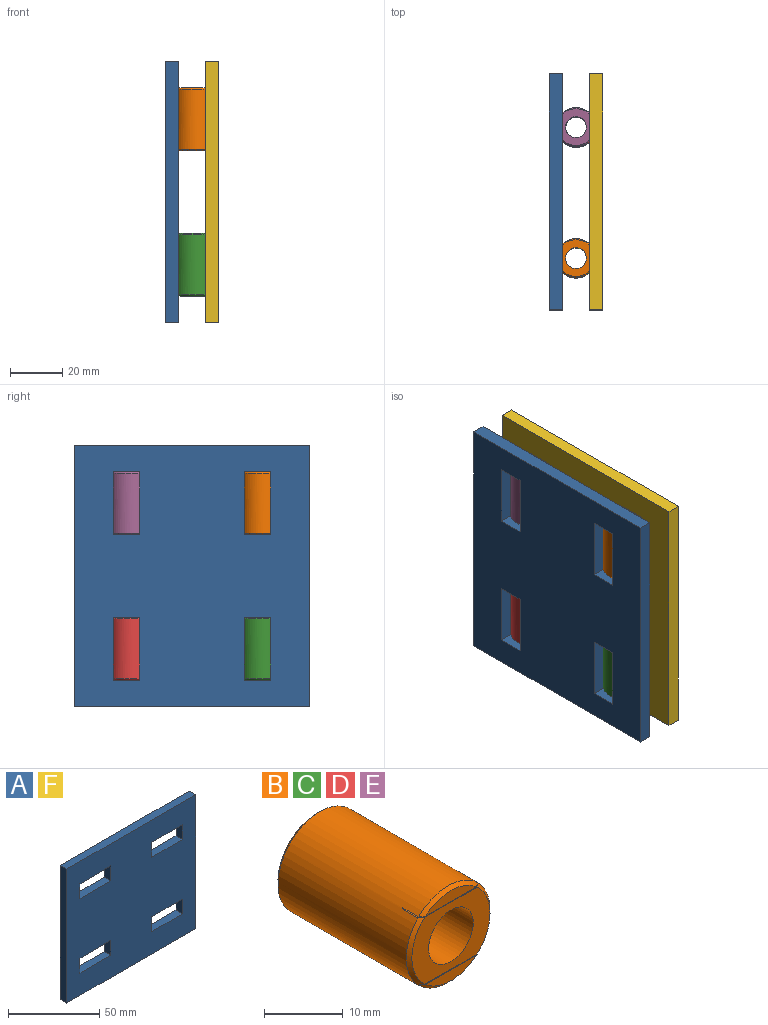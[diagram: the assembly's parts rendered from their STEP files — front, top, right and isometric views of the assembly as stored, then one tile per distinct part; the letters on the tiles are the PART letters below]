
ASSEMBLY  parts=6 mates=7
PART A: 22 faces, bbox 100x5x90 mm
  f0: plane 100x5mm, normal (0,0,1), area 500mm2, adj f1,f19,f20,f21
  f1: plane 90x5mm, normal (-1,0,0), area 450mm2, adj f0,f2,f20,f21
  f2: plane 100x5mm, normal (0,0,-1), area 500mm2, adj f1,f19,f20,f21
  f3: plane 24x5mm, normal (0,0,1), area 120mm2, adj f4,f15,f20,f21
  f4: plane 10x5mm, normal (1,0,0), area 50mm2, adj f3,f5,f20,f21
  f5: plane 24x5mm, normal (0,0,-1), area 120mm2, adj f4,f15,f20,f21
  f6: plane 24x5mm, normal (0,0,1), area 120mm2, adj f7,f16,f20,f21
  f7: plane 10x5mm, normal (1,0,0), area 50mm2, adj f6,f8,f20,f21
  f8: plane 24x5mm, normal (0,0,-1), area 120mm2, adj f7,f16,f20,f21
  f9: plane 24x5mm, normal (0,0,-1), area 120mm2, adj f10,f17,f20,f21
  f10: plane 10x5mm, normal (-1,0,0), area 50mm2, adj f9,f11,f20,f21
  f11: plane 24x5mm, normal (0,0,1), area 120mm2, adj f10,f17,f20,f21
  f12: plane 24x5mm, normal (0,0,1), area 120mm2, adj f13,f18,f20,f21
  f13: plane 10x5mm, normal (1,0,0), area 50mm2, adj f12,f14,f20,f21
  f14: plane 24x5mm, normal (0,0,-1), area 120mm2, adj f13,f18,f20,f21
  f15: plane 10x5mm, normal (-1,0,0), area 50mm2, adj f3,f5,f20,f21
  f16: plane 10x5mm, normal (-1,0,0), area 50mm2, adj f6,f8,f20,f21
  f17: plane 10x5mm, normal (1,0,0), area 50mm2, adj f9,f11,f20,f21
  f18: plane 10x5mm, normal (-1,0,0), area 50mm2, adj f12,f14,f20,f21
  f19: plane 90x5mm, normal (1,0,0), area 450mm2, adj f0,f2,f20,f21
  f20: plane 100x90mm, normal (0,-1,0), area 8040mm2, adj f0,f1,f2,f3,f4,f5,f6,f7
  f21: plane 100x90mm, normal (0,1,0), area 8040mm2, adj f0,f1,f2,f3,f4,f5,f6,f7
PART B: 17 faces, bbox 15x24x15 mm
  f0: plane 9.15x1.7mm, normal (0,-1,0), area 10.6mm2, adj f1,f16
  f1: cone r=7mm half-angle=45deg, axis (0,1,0), area 7.7mm2, adj f0,f6,f16
  f2: cone r=7mm half-angle=45deg, axis (0,1,0), area 8.2mm2, adj f6,f7,f12,f15
  f3: plane 9.15x1.7mm, normal (0,-1,0), area 10.6mm2, adj f4,f13
  f4: cone r=7mm half-angle=45deg, axis (0,1,0), area 7.7mm2, adj f3,f6,f13
  f5: cylinder r=4mm len=24mm, axis (0,1,0), area 603.2mm2, adj f7,f8
  f6: cylinder r=7.5mm len=23mm, axis (0,1,0), area 1082.3mm2, adj f1,f2,f4,f9,f10,f11,f12,f13
  f7: plane 14x10.4mm, normal (0,-1,0), area 80.5mm2, adj f2,f5,f9,f12,f15
  f8: plane 14x14mm, normal (0,1,0), area 103.7mm2, adj f5,f10
  f9: cone r=7mm half-angle=45deg, axis (0,1,0), area 8.2mm2, adj f6,f7,f12,f15
  f10: cone r=7.5mm half-angle=45deg, axis (0,-1,0), area 32.2mm2, adj f6,f8
  f11: plane 10.81x0.1mm, normal (0,-1,0), area 1.1mm2, adj f6,f12,f13
  f12: plane 10.83x3.34mm, normal (0,0,-1), area 35.5mm2, adj f2,f6,f7,f9,f11
  f13: plane 10.64x3.34mm, normal (0,0,1), area 34.9mm2, adj f3,f4,f6,f11
  f14: plane 10.81x0.1mm, normal (0,-1,0), area 1.1mm2, adj f6,f15,f16
  f15: plane 10.83x3.34mm, normal (0,0,1), area 35.5mm2, adj f2,f6,f7,f9,f14
  f16: plane 10.64x3.34mm, normal (0,0,-1), area 34.9mm2, adj f0,f1,f6,f14
PART C: same geometry as B
PART D: same geometry as B
PART E: same geometry as B
PART F: same geometry as A
PLACE A rot(axis=(-0.58,-0.58,-0.58),120deg) t=(-125.64,-76,-25.35)mm
PLACE B rot(axis=(-0.58,0.58,-0.58),120deg) t=(-120.44,-56.31,40.43)mm
PLACE C rot(axis=(-0.58,0.58,-0.58),120deg) t=(-120.44,-56.31,-15.13)mm
PLACE D rot(axis=(-0.58,0.58,-0.58),120deg) t=(-120.34,-6.43,-15.13)mm
PLACE E rot(axis=(-0.58,0.58,-0.58),120deg) t=(-120.44,-6.31,40.43)mm
PLACE F rot(axis=(-0.58,-0.58,-0.58),120deg) t=(-110.24,-76,-25.35)mm
MATE fastened B.f7 <-> A.f18  axis (0,0,1) through (-125.64,-61,64.43)mm
MATE fastened D.f3 <-> A.f15  axis (0,0,1) through (-125.64,-11,8.87)mm
MATE fastened B.f7 <-> F.f18  axis (0,0,1) through (-115.24,-61,64.43)mm
MATE parallel F.f19 <-> A.f19  axis (0,0,1) through (-112.74,-31,74.65)mm
MATE fastened C.f7 <-> A.f16  axis (0,0,1) through (-125.64,-61,8.87)mm
MATE parallel A.f21 <-> F.f20  axis (1,0,0) through (-125.64,-31,24.65)mm
MATE fastened E.f7 <-> A.f10  axis (0,0,1) through (-125.64,-11,64.43)mm
